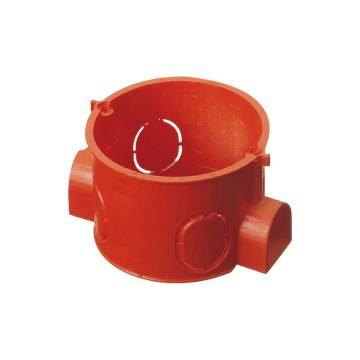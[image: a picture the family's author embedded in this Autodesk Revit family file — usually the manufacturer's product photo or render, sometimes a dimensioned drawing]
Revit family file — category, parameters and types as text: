
# Revit family: Building-FlushMountingEnclosures-GEWISS-24SC-BOXES_ROUND_MODULAR
name_source: partatom
category: Apparecchi elettrici
revit_build: Autodesk Revit 2016 (Build: 20161004_0715(x64)
units: mm (PartAtom-declared; Revit-internal decimal feet)

## family parameters
Condiviso = Sì
Host = Muro
Mantenere orientamento annotazione = Sì
Numero OmniClass = 23.80.30.14.24
Punto di calcolo locali = Sì
Quota connettore circolare = Usa diametro
Sempre verticale = Sì
Taglio con vuoti quando caricato = Sì
Tipo di parte = Normale
Titolo OmniClass = Junction Boxes

## types (1)
- GW24232 - Sectional round box
    Catalogue = BUILDING
    Catalogue Range = 24SC
    Characteristics = Halogen free
    Description: = Modular round
    Descrizione = SECTIONAL ROUND BOX
    Dimensions (mm) = Ã˜ 60 x 42
    EAN code = 8011564072312
    Electrocod = 0210
    Fixing supports axles distance = 60MM
    For walls = Masonry
    Glow Wire Test = 650°C
    IDF = 0d95521e-4609-4240-9dad-304ee1fb8deb
    IDT = d3faba48-2ce0-441e-8284-55e0996afa80
    Immagine tipo = GW24232.jpg
    Installation = Flush mounting enclosures
    Modello = GW24232
    Operating temperature = -15 ÷ +60°C
    Produttore = GEWISS S.p.A.
    SEO = Box
    Technical sheet = https://www.gewiss.com
    Thermo-pressure with ball = 70
    URL = https://www.gewiss.com
    Version file RFA = 19.0

note: source unit labels omitted for Thermo-pressure with ball — the stored unit's dimension contradicts the parameter name (converter mislabeling)
